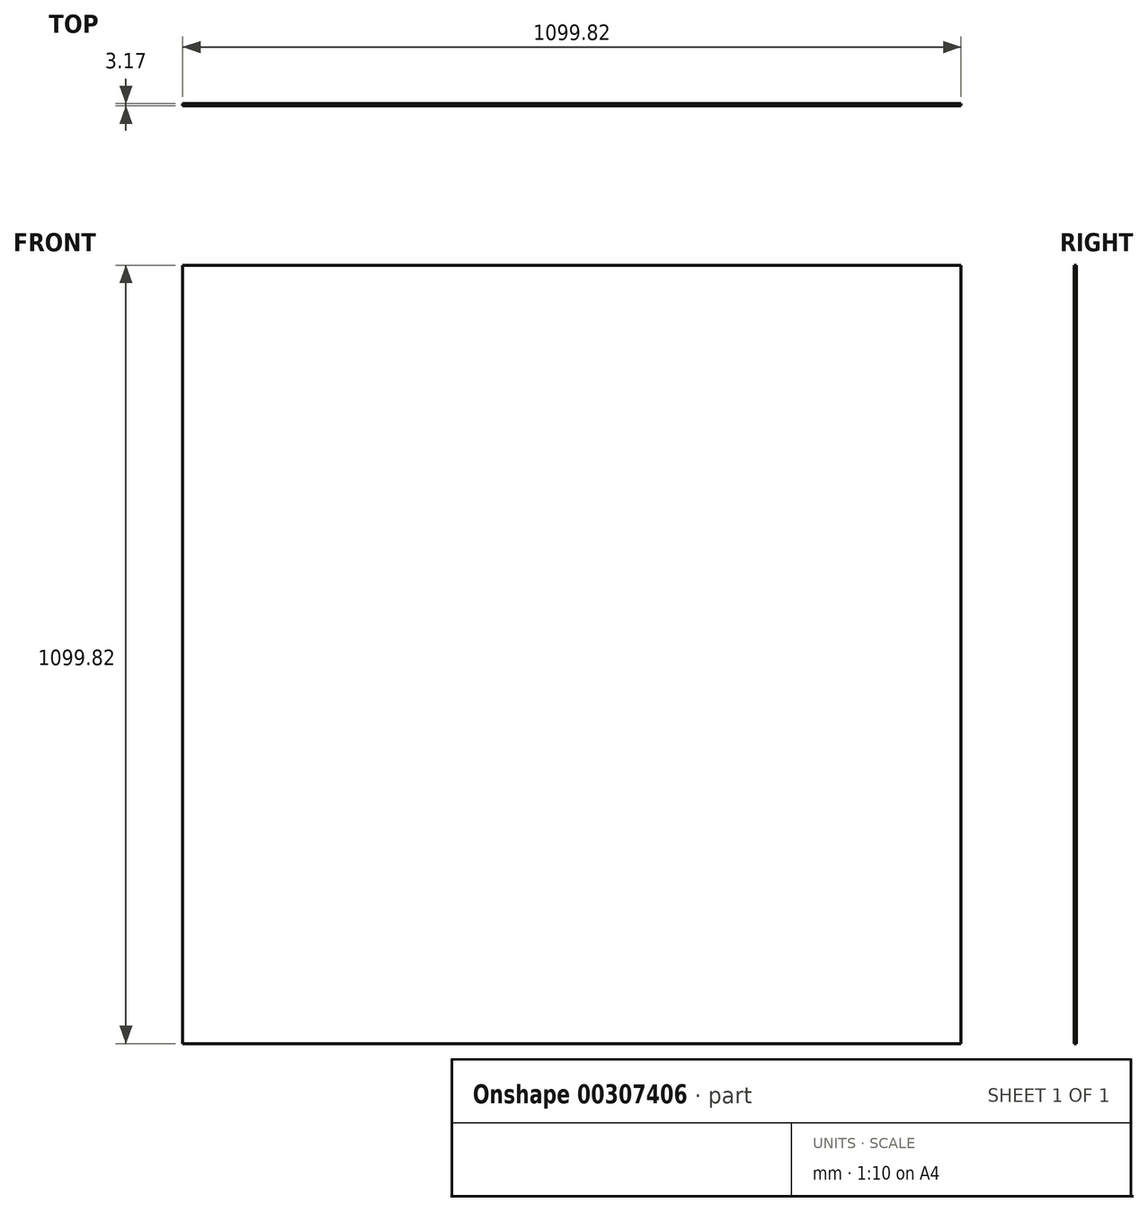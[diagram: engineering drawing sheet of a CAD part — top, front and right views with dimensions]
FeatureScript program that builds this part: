
annotation { "Feature Type Name" : "Feature", "Feature Type Description" : "" }
export const myFeature = defineFeature(function(context is Context, id is Id, definition is map)
    precondition{}
    {
        {
            var Q0;
            Q0=qCreatedBy(makeId("Front.planeOp"),FACE);
            var sketch = newSketch(context, id + "F0", { "sketchPlane" : qUnion([Q0])});
            skLineSegment(sketch, "E0.bottom", {"start": v(549.9, 549.9) * mm, "end": v(-549.91, 549.9) * mm});
            skLineSegment(sketch, "E0.top", {"start": v(549.9, -549.9) * mm, "end": v(-549.9, -549.9) * mm});
            skLineSegment(sketch, "E0.left", {"start": v(549.9, 549.9) * mm, "end": v(549.9, -549.9) * mm});
            skLineSegment(sketch, "E0.right", {"start": v(-549.9, 549.9) * mm, "end": v(-549.9, -549.9) * mm});
            skPoint(sketch, "E0.middle", {"position": v(0, 0) * mm});
            skSolve(sketch);
        }
        {
            var Q0;
            Q0=qSketchRegion(id+"F0",true);
            extrude(context, id + "F1", {"entities" : qUnion([Q0]), "depth" : 3.17 * mm});
        }
    });
